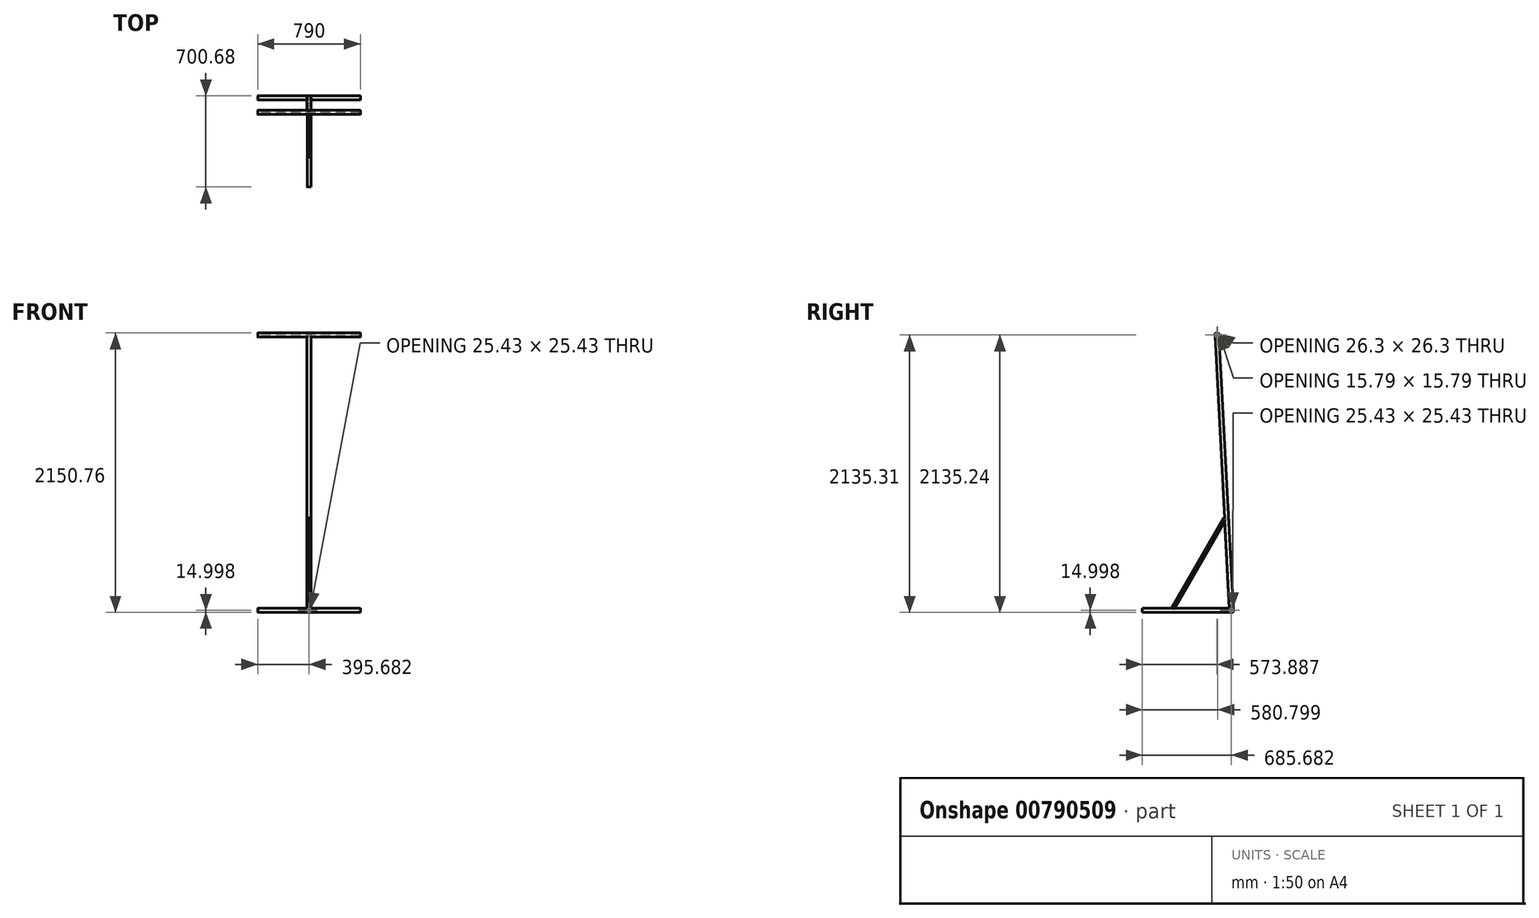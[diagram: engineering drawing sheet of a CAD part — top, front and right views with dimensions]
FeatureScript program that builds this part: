
annotation { "Feature Type Name" : "Feature", "Feature Type Description" : "" }
export const myFeature = defineFeature(function(context is Context, id is Id, definition is map)
    precondition{}
    {
        {
            var Q0;
            Q0=qCreatedBy(makeId("Top.planeOp"),FACE);
            var sketch = newSketch(context, id + "F0", { "sketchPlane" : qUnion([Q0])});
            skLineSegment(sketch, "E0.bottom", {"start": v(-8.65, 15) * mm, "end": v(8.65, 15) * mm});
            skLineSegment(sketch, "E0.top", {"start": v(-8.65, -15) * mm, "end": v(8.65, -15) * mm});
            skLineSegment(sketch, "E0.left", {"start": v(-15, 8.65) * mm, "end": v(-15, -8.65) * mm});
            skLineSegment(sketch, "E0.right", {"start": v(15, 8.65) * mm, "end": v(15, -8.65) * mm});
            skPoint(sketch, "E1", {"position": v(-15, 0) * mm});
            skPoint(sketch, "E2", {"position": v(0, 15) * mm});
            skPoint(sketch, "E3.visualSharp", {"position": v(-15, 15) * mm});
            skArc(sketch, "E3.filletArc", {"start": v(-8.65, 15) * mm, "mid": v(-13.14, 13.14) * mm, "end": v(-15, 8.65) * mm});
            skPoint(sketch, "E4.visualSharp", {"position": v(15, 15) * mm});
            skArc(sketch, "E4.filletArc", {"start": v(15, 8.65) * mm, "mid": v(13.14, 13.14) * mm, "end": v(8.65, 15) * mm});
            skPoint(sketch, "E5.visualSharp", {"position": v(15, -15) * mm});
            skArc(sketch, "E5.filletArc", {"start": v(8.65, -15) * mm, "mid": v(13.14, -13.14) * mm, "end": v(15, -8.65) * mm});
            skPoint(sketch, "E6.visualSharp", {"position": v(-15, -15) * mm});
            skArc(sketch, "E6.filletArc", {"start": v(-15, -8.65) * mm, "mid": v(-13.14, -13.14) * mm, "end": v(-8.65, -15) * mm});
            skArc(sketch, "E7.0", {"start": v(-8.65, 12.71) * mm, "mid": v(-11.52, 11.52) * mm, "end": v(-12.71, 8.65) * mm});
            skLineSegment(sketch, "E7.1", {"start": v(-8.65, 12.71) * mm, "end": v(8.65, 12.71) * mm});
            skLineSegment(sketch, "E7.2", {"start": v(-12.71, 8.65) * mm, "end": v(-12.71, -8.65) * mm});
            skArc(sketch, "E7.3", {"start": v(12.71, 8.65) * mm, "mid": v(11.52, 11.52) * mm, "end": v(8.65, 12.71) * mm});
            skArc(sketch, "E7.4", {"start": v(-12.71, -8.65) * mm, "mid": v(-11.52, -11.52) * mm, "end": v(-8.65, -12.71) * mm});
            skLineSegment(sketch, "E7.5", {"start": v(-8.65, -12.71) * mm, "end": v(8.65, -12.71) * mm});
            skArc(sketch, "E7.6", {"start": v(8.65, -12.71) * mm, "mid": v(11.52, -11.52) * mm, "end": v(12.71, -8.65) * mm});
            skLineSegment(sketch, "E7.7", {"start": v(12.71, 8.65) * mm, "end": v(12.71, -8.65) * mm});
            skSolve(sketch);
        }
        {
            var Q0;
            Q0=makeQuery(id+"F0.imprint","IMPRINT",FACE,{"disambiguationData":[TD([[makeQuery(id+"F0.imprint","IMPRINT",EDGE,{"derivedFrom":sQuery(id+"F0.wireOp",EDGE,"E0.bottom")}),-1.0]])]});
            extrude(context, id + "F1", {"entities" : qUnion([Q0]), "depth" : 2130 * mm, "offsetDistance" : 25.4 * mm});
        }
        {
            var Q0;
            Q0=makeQuery(id+"F1.opExtrude","SWEPT_BODY",BODY,{"disambiguationData":[OSD([sQuery(id+"F0.wireOp",EDGE,"E0.bottom"),sQuery(id+"F0.wireOp",EDGE,"E0.top"),sQuery(id+"F0.wireOp",EDGE,"E0.left"),sQuery(id+"F0.wireOp",EDGE,"E0.right"),sQuery(id+"F0.wireOp",EDGE,"E3.filletArc"),sQuery(id+"F0.wireOp",EDGE,"E4.filletArc"),sQuery(id+"F0.wireOp",EDGE,"E5.filletArc"),sQuery(id+"F0.wireOp",EDGE,"E6.filletArc"),sQuery(id+"F0.wireOp",EDGE,"E7.0"),sQuery(id+"F0.wireOp",EDGE,"E7.1"),sQuery(id+"F0.wireOp",EDGE,"E7.2"),sQuery(id+"F0.wireOp",EDGE,"E7.3"),sQuery(id+"F0.wireOp",EDGE,"E7.4"),sQuery(id+"F0.wireOp",EDGE,"E7.5"),sQuery(id+"F0.wireOp",EDGE,"E7.6"),sQuery(id+"F0.wireOp",EDGE,"E7.7")])]});
            var Q1;
            Q1=makeQuery(id+"F1.opExtrude","CAP_EDGE",EDGE,{"disambiguationData":[OSD([sQuery(id+"F0.wireOp",EDGE,"E0.top")])],"isStart":true});
            transform(context, id + "F2", {"entities" : qUnion([Q0]), "transformType" : TransformType.ROTATION, "transformAxis" : qUnion([Q1]), "angle" : 3 * degree, "makeCopy" : false});
        }
        {
            var Q0;
            Q0=qCreatedBy(makeId("Right.planeOp"),FACE);
            var sketch = newSketch(context, id + "F3", { "sketchPlane" : qUnion([Q0])});
            skLineSegment(sketch, "E8.bottom", {"start": v(-7.97, 14.32) * mm, "end": v(9.33, 14.32) * mm});
            skLineSegment(sketch, "E8.top", {"start": v(-7.97, -15.68) * mm, "end": v(9.33, -15.68) * mm});
            skLineSegment(sketch, "E8.left", {"start": v(-14.32, 7.97) * mm, "end": v(-14.32, -9.33) * mm});
            skLineSegment(sketch, "E8.right", {"start": v(15.68, 7.97) * mm, "end": v(15.68, -9.33) * mm});
            skPoint(sketch, "E9", {"position": v(-14.32, -0.68) * mm});
            skPoint(sketch, "E10", {"position": v(0.68, 14.32) * mm});
            skPoint(sketch, "E11.visualSharp", {"position": v(-14.32, 14.32) * mm});
            skArc(sketch, "E11.filletArc", {"start": v(-7.97, 14.32) * mm, "mid": v(-12.46, 12.46) * mm, "end": v(-14.32, 7.97) * mm});
            skPoint(sketch, "E12.visualSharp", {"position": v(15.68, 14.32) * mm});
            skArc(sketch, "E12.filletArc", {"start": v(15.68, 7.97) * mm, "mid": v(13.82, 12.46) * mm, "end": v(9.33, 14.32) * mm});
            skPoint(sketch, "E13.visualSharp", {"position": v(15.68, -15.68) * mm});
            skArc(sketch, "E13.filletArc", {"start": v(9.33, -15.68) * mm, "mid": v(13.82, -13.82) * mm, "end": v(15.68, -9.33) * mm});
            skPoint(sketch, "E14.visualSharp", {"position": v(-14.32, -15.68) * mm});
            skArc(sketch, "E14.filletArc", {"start": v(-14.32, -9.33) * mm, "mid": v(-12.46, -13.82) * mm, "end": v(-7.97, -15.68) * mm});
            skArc(sketch, "E15.0", {"start": v(-7.97, 12.03) * mm, "mid": v(-10.84, 10.84) * mm, "end": v(-12.03, 7.97) * mm});
            skLineSegment(sketch, "E15.1", {"start": v(-7.97, 12.03) * mm, "end": v(9.33, 12.03) * mm});
            skLineSegment(sketch, "E15.2", {"start": v(-12.03, 7.97) * mm, "end": v(-12.03, -9.33) * mm});
            skArc(sketch, "E15.3", {"start": v(13.4, 7.97) * mm, "mid": v(12.2, 10.84) * mm, "end": v(9.33, 12.03) * mm});
            skArc(sketch, "E15.4", {"start": v(-12.03, -9.33) * mm, "mid": v(-10.84, -12.2) * mm, "end": v(-7.97, -13.4) * mm});
            skLineSegment(sketch, "E15.5", {"start": v(-7.97, -13.4) * mm, "end": v(9.33, -13.4) * mm});
            skArc(sketch, "E15.6", {"start": v(9.33, -13.4) * mm, "mid": v(12.2, -12.2) * mm, "end": v(13.4, -9.33) * mm});
            skLineSegment(sketch, "E15.7", {"start": v(13.4, 7.97) * mm, "end": v(13.4, -9.33) * mm});
            skSolve(sketch);
        }
        {
            var Q0;
            Q0=makeQuery(id+"F3.imprint","IMPRINT",FACE,{"disambiguationData":[TD([[makeQuery(id+"F3.imprint","IMPRINT",EDGE,{"derivedFrom":sQuery(id+"F3.wireOp",EDGE,"E8.bottom")}),-1.0]])]});
            extrude(context, id + "F4", {"entities" : qUnion([Q0]), "depth" : 790 * mm, "offsetDistance" : 25.4 * mm});
        }
        {
            var Q0;
            Q0=makeQuery(id+"F4.opExtrude","SWEPT_BODY",BODY,{"disambiguationData":[OSD([sQuery(id+"F3.wireOp",EDGE,"E8.bottom"),sQuery(id+"F3.wireOp",EDGE,"E8.top"),sQuery(id+"F3.wireOp",EDGE,"E8.left"),sQuery(id+"F3.wireOp",EDGE,"E8.right"),sQuery(id+"F3.wireOp",EDGE,"E11.filletArc"),sQuery(id+"F3.wireOp",EDGE,"E12.filletArc"),sQuery(id+"F3.wireOp",EDGE,"E13.filletArc"),sQuery(id+"F3.wireOp",EDGE,"E14.filletArc"),sQuery(id+"F3.wireOp",EDGE,"E15.0"),sQuery(id+"F3.wireOp",EDGE,"E15.1"),sQuery(id+"F3.wireOp",EDGE,"E15.2"),sQuery(id+"F3.wireOp",EDGE,"E15.3"),sQuery(id+"F3.wireOp",EDGE,"E15.4"),sQuery(id+"F3.wireOp",EDGE,"E15.5"),sQuery(id+"F3.wireOp",EDGE,"E15.6"),sQuery(id+"F3.wireOp",EDGE,"E15.7")])]});
            transform(context, id + "F5", {"entities" : qUnion([Q0]), "transformType" : TransformType.TRANSLATION_3D, "dx" : -395 * mm, "dy" : 0 * mm, "dz" : 0 * mm, "makeCopy" : false});
        }
        {
            var Q0;
            Q0=makeQuery(id+"F4.opExtrude","SWEPT_BODY",BODY,{"disambiguationData":[OSD([sQuery(id+"F3.wireOp",EDGE,"E8.bottom"),sQuery(id+"F3.wireOp",EDGE,"E8.top"),sQuery(id+"F3.wireOp",EDGE,"E8.left"),sQuery(id+"F3.wireOp",EDGE,"E8.right"),sQuery(id+"F3.wireOp",EDGE,"E11.filletArc"),sQuery(id+"F3.wireOp",EDGE,"E12.filletArc"),sQuery(id+"F3.wireOp",EDGE,"E13.filletArc"),sQuery(id+"F3.wireOp",EDGE,"E14.filletArc"),sQuery(id+"F3.wireOp",EDGE,"E15.0"),sQuery(id+"F3.wireOp",EDGE,"E15.1"),sQuery(id+"F3.wireOp",EDGE,"E15.2"),sQuery(id+"F3.wireOp",EDGE,"E15.3"),sQuery(id+"F3.wireOp",EDGE,"E15.4"),sQuery(id+"F3.wireOp",EDGE,"E15.5"),sQuery(id+"F3.wireOp",EDGE,"E15.6"),sQuery(id+"F3.wireOp",EDGE,"E15.7")])]});
            transform(context, id + "F6", {"entities" : qUnion([Q0]), "transformType" : TransformType.TRANSLATION_3D, "dx" : 0 * mm, "dy" : 0 * mm, "dz" : 0 * mm, "makeCopy" : true});
        }
        {
            var Q0;
            Q0=makeQuery(id+"F6.opPattern","COPY",BODY,{"derivedFrom":makeQuery(id+"F4.opExtrude","SWEPT_BODY",BODY,{"disambiguationData":[OSD([sQuery(id+"F3.wireOp",EDGE,"E8.bottom"),sQuery(id+"F3.wireOp",EDGE,"E8.top"),sQuery(id+"F3.wireOp",EDGE,"E8.left"),sQuery(id+"F3.wireOp",EDGE,"E8.right"),sQuery(id+"F3.wireOp",EDGE,"E11.filletArc"),sQuery(id+"F3.wireOp",EDGE,"E12.filletArc"),sQuery(id+"F3.wireOp",EDGE,"E13.filletArc"),sQuery(id+"F3.wireOp",EDGE,"E14.filletArc"),sQuery(id+"F3.wireOp",EDGE,"E15.0"),sQuery(id+"F3.wireOp",EDGE,"E15.1"),sQuery(id+"F3.wireOp",EDGE,"E15.2"),sQuery(id+"F3.wireOp",EDGE,"E15.3"),sQuery(id+"F3.wireOp",EDGE,"E15.4"),sQuery(id+"F3.wireOp",EDGE,"E15.5"),sQuery(id+"F3.wireOp",EDGE,"E15.6"),sQuery(id+"F3.wireOp",EDGE,"E15.7")])]}),"instanceName":"1"});
            var Q1;
            Q1=makeQuery(id+"F6.opPattern","COPY",EDGE,{"derivedFrom":makeQuery(id+"F4.opExtrude","SWEPT_EDGE",EDGE,{"disambiguationData":[OSD([sQuery(id+"F3.wireOp",EDGE,"E8.top"),sQuery(id+"F3.wireOp",EDGE,"E14.filletArc")])]}),"instanceName":"1"});
            transform(context, id + "F7", {"entities" : qUnion([Q0]), "transformType" : TransformType.ROTATION, "transformAxis" : qUnion([Q1]), "angle" : 357 * degree, "makeCopy" : false});
        }
        {
            var Q0;
            Q0=makeQuery(id+"F6.opPattern","COPY",BODY,{"derivedFrom":makeQuery(id+"F4.opExtrude","SWEPT_BODY",BODY,{"disambiguationData":[OSD([sQuery(id+"F3.wireOp",EDGE,"E8.bottom"),sQuery(id+"F3.wireOp",EDGE,"E8.top"),sQuery(id+"F3.wireOp",EDGE,"E8.left"),sQuery(id+"F3.wireOp",EDGE,"E8.right"),sQuery(id+"F3.wireOp",EDGE,"E11.filletArc"),sQuery(id+"F3.wireOp",EDGE,"E12.filletArc"),sQuery(id+"F3.wireOp",EDGE,"E13.filletArc"),sQuery(id+"F3.wireOp",EDGE,"E14.filletArc"),sQuery(id+"F3.wireOp",EDGE,"E15.0"),sQuery(id+"F3.wireOp",EDGE,"E15.1"),sQuery(id+"F3.wireOp",EDGE,"E15.2"),sQuery(id+"F3.wireOp",EDGE,"E15.3"),sQuery(id+"F3.wireOp",EDGE,"E15.4"),sQuery(id+"F3.wireOp",EDGE,"E15.5"),sQuery(id+"F3.wireOp",EDGE,"E15.6"),sQuery(id+"F3.wireOp",EDGE,"E15.7")])]}),"instanceName":"1"});
            transform(context, id + "F8", {"entities" : qUnion([Q0]), "transformType" : TransformType.TRANSLATION_3D, "dx" : 0 * mm, "dy" : -111 * mm, "dz" : 2119.88 * mm, "makeCopy" : false});
        }
        {
            var Q0;
            Q0=qCreatedBy(makeId("Right.planeOp"),FACE);
            var sketch = newSketch(context, id + "F9", { "sketchPlane" : qUnion([Q0])});
            skLineSegment(sketch, "E16.bottom", {"start": v(2.03, 14.32) * mm, "end": v(9.33, 14.32) * mm});
            skLineSegment(sketch, "E16.top", {"start": v(2.03, -5.68) * mm, "end": v(9.33, -5.68) * mm});
            skLineSegment(sketch, "E16.left", {"start": v(-4.32, 7.97) * mm, "end": v(-4.32, 0.67) * mm});
            skLineSegment(sketch, "E16.right", {"start": v(15.68, 7.97) * mm, "end": v(15.68, 0.67) * mm});
            skPoint(sketch, "E17", {"position": v(-4.32, 4.32) * mm});
            skPoint(sketch, "E18", {"position": v(5.68, 14.32) * mm});
            skPoint(sketch, "E19.visualSharp", {"position": v(-4.32, 14.32) * mm});
            skArc(sketch, "E19.filletArc", {"start": v(2.03, 14.32) * mm, "mid": v(-2.46, 12.46) * mm, "end": v(-4.32, 7.97) * mm});
            skPoint(sketch, "E20.visualSharp", {"position": v(15.68, 14.32) * mm});
            skArc(sketch, "E20.filletArc", {"start": v(15.68, 7.97) * mm, "mid": v(13.82, 12.46) * mm, "end": v(9.33, 14.32) * mm});
            skPoint(sketch, "E21.visualSharp", {"position": v(15.68, -5.68) * mm});
            skArc(sketch, "E21.filletArc", {"start": v(9.33, -5.68) * mm, "mid": v(13.82, -3.82) * mm, "end": v(15.68, 0.67) * mm});
            skPoint(sketch, "E22.visualSharp", {"position": v(-4.32, -5.68) * mm});
            skArc(sketch, "E22.filletArc", {"start": v(-4.32, 0.67) * mm, "mid": v(-2.46, -3.82) * mm, "end": v(2.03, -5.68) * mm});
            skArc(sketch, "E23.0", {"start": v(2.03, 12.03) * mm, "mid": v(-0.84, 10.84) * mm, "end": v(-2.03, 7.97) * mm});
            skLineSegment(sketch, "E23.1", {"start": v(2.03, 12.03) * mm, "end": v(9.33, 12.03) * mm});
            skLineSegment(sketch, "E23.2", {"start": v(-2.03, 7.97) * mm, "end": v(-2.03, 0.67) * mm});
            skArc(sketch, "E23.3", {"start": v(13.4, 7.97) * mm, "mid": v(12.2, 10.84) * mm, "end": v(9.33, 12.03) * mm});
            skArc(sketch, "E23.4", {"start": v(-2.03, 0.67) * mm, "mid": v(-0.84, -2.2) * mm, "end": v(2.03, -3.4) * mm});
            skLineSegment(sketch, "E23.5", {"start": v(2.03, -3.4) * mm, "end": v(9.33, -3.4) * mm});
            skArc(sketch, "E23.6", {"start": v(9.33, -3.4) * mm, "mid": v(12.2, -2.2) * mm, "end": v(13.4, 0.67) * mm});
            skLineSegment(sketch, "E23.7", {"start": v(13.4, 7.97) * mm, "end": v(13.4, 0.67) * mm});
            skSolve(sketch);
        }
        {
            var Q0;
            Q0=makeQuery(id+"F9.imprint","IMPRINT",FACE,{"disambiguationData":[TD([[makeQuery(id+"F9.imprint","IMPRINT",EDGE,{"derivedFrom":sQuery(id+"F9.wireOp",EDGE,"E16.bottom")}),-1.0]])]});
            extrude(context, id + "F10", {"entities" : qUnion([Q0]), "depth" : 790 * mm, "offsetDistance" : 25.4 * mm});
        }
        {
            var Q0;
            Q0=makeQuery(id+"F10.opExtrude","SWEPT_BODY",BODY,{"disambiguationData":[OSD([sQuery(id+"F9.wireOp",EDGE,"E16.bottom"),sQuery(id+"F9.wireOp",EDGE,"E16.top"),sQuery(id+"F9.wireOp",EDGE,"E16.left"),sQuery(id+"F9.wireOp",EDGE,"E16.right"),sQuery(id+"F9.wireOp",EDGE,"E19.filletArc"),sQuery(id+"F9.wireOp",EDGE,"E20.filletArc"),sQuery(id+"F9.wireOp",EDGE,"E21.filletArc"),sQuery(id+"F9.wireOp",EDGE,"E22.filletArc"),sQuery(id+"F9.wireOp",EDGE,"E23.0"),sQuery(id+"F9.wireOp",EDGE,"E23.1"),sQuery(id+"F9.wireOp",EDGE,"E23.2"),sQuery(id+"F9.wireOp",EDGE,"E23.3"),sQuery(id+"F9.wireOp",EDGE,"E23.4"),sQuery(id+"F9.wireOp",EDGE,"E23.5"),sQuery(id+"F9.wireOp",EDGE,"E23.6"),sQuery(id+"F9.wireOp",EDGE,"E23.7")])]});
            transform(context, id + "F11", {"entities" : qUnion([Q0]), "transformType" : TransformType.TRANSLATION_3D, "dx" : -395 * mm, "dy" : 0 * mm, "dz" : 0 * mm, "makeCopy" : false});
        }
        {
            var Q0;
            Q0=makeQuery(id+"F10.opExtrude","SWEPT_BODY",BODY,{"disambiguationData":[OSD([sQuery(id+"F9.wireOp",EDGE,"E16.bottom"),sQuery(id+"F9.wireOp",EDGE,"E16.top"),sQuery(id+"F9.wireOp",EDGE,"E16.left"),sQuery(id+"F9.wireOp",EDGE,"E16.right"),sQuery(id+"F9.wireOp",EDGE,"E19.filletArc"),sQuery(id+"F9.wireOp",EDGE,"E20.filletArc"),sQuery(id+"F9.wireOp",EDGE,"E21.filletArc"),sQuery(id+"F9.wireOp",EDGE,"E22.filletArc"),sQuery(id+"F9.wireOp",EDGE,"E23.0"),sQuery(id+"F9.wireOp",EDGE,"E23.1"),sQuery(id+"F9.wireOp",EDGE,"E23.2"),sQuery(id+"F9.wireOp",EDGE,"E23.3"),sQuery(id+"F9.wireOp",EDGE,"E23.4"),sQuery(id+"F9.wireOp",EDGE,"E23.5"),sQuery(id+"F9.wireOp",EDGE,"E23.6"),sQuery(id+"F9.wireOp",EDGE,"E23.7")])]});
            transform(context, id + "F12", {"entities" : qUnion([Q0]), "transformType" : TransformType.TRANSLATION_3D, "dx" : 0 * mm, "dy" : -109.47 * mm, "dz" : 2115.06 * mm, "makeCopy" : false});
        }
        {
            var Q0;
            Q0=makeQuery(id+"F10.opExtrude","SWEPT_BODY",BODY,{"disambiguationData":[OSD([sQuery(id+"F9.wireOp",EDGE,"E16.bottom"),sQuery(id+"F9.wireOp",EDGE,"E16.top"),sQuery(id+"F9.wireOp",EDGE,"E16.left"),sQuery(id+"F9.wireOp",EDGE,"E16.right"),sQuery(id+"F9.wireOp",EDGE,"E19.filletArc"),sQuery(id+"F9.wireOp",EDGE,"E20.filletArc"),sQuery(id+"F9.wireOp",EDGE,"E21.filletArc"),sQuery(id+"F9.wireOp",EDGE,"E22.filletArc"),sQuery(id+"F9.wireOp",EDGE,"E23.0"),sQuery(id+"F9.wireOp",EDGE,"E23.1"),sQuery(id+"F9.wireOp",EDGE,"E23.2"),sQuery(id+"F9.wireOp",EDGE,"E23.3"),sQuery(id+"F9.wireOp",EDGE,"E23.4"),sQuery(id+"F9.wireOp",EDGE,"E23.5"),sQuery(id+"F9.wireOp",EDGE,"E23.6"),sQuery(id+"F9.wireOp",EDGE,"E23.7")])]});
            var Q1;
            Q1=makeQuery(id+"F10.opExtrude","SWEPT_EDGE",EDGE,{"disambiguationData":[OSD([sQuery(id+"F9.wireOp",EDGE,"E23.4"),sQuery(id+"F9.wireOp",EDGE,"E23.5")])]});
            transform(context, id + "F13", {"entities" : qUnion([Q0]), "transformType" : TransformType.ROTATION, "transformAxis" : qUnion([Q1]), "angle" : 357 * degree, "makeCopy" : false});
        }
        {
            var Q0;
            Q0=qCreatedBy(makeId("Front.planeOp"),FACE);
            var sketch = newSketch(context, id + "F14", { "sketchPlane" : qUnion([Q0])});
            skLineSegment(sketch, "E24.bottom", {"start": v(-7.97, 14.32) * mm, "end": v(9.33, 14.32) * mm});
            skLineSegment(sketch, "E24.top", {"start": v(-7.97, -15.68) * mm, "end": v(9.33, -15.68) * mm});
            skLineSegment(sketch, "E24.left", {"start": v(-14.32, 7.97) * mm, "end": v(-14.32, -9.33) * mm});
            skLineSegment(sketch, "E24.right", {"start": v(15.68, 7.97) * mm, "end": v(15.68, -9.33) * mm});
            skPoint(sketch, "E25", {"position": v(-14.32, -0.68) * mm});
            skPoint(sketch, "E26", {"position": v(0.68, 14.32) * mm});
            skPoint(sketch, "E27.visualSharp", {"position": v(-14.32, 14.32) * mm});
            skArc(sketch, "E27.filletArc", {"start": v(-7.97, 14.32) * mm, "mid": v(-12.46, 12.46) * mm, "end": v(-14.32, 7.97) * mm});
            skPoint(sketch, "E28.visualSharp", {"position": v(15.68, 14.32) * mm});
            skArc(sketch, "E28.filletArc", {"start": v(15.68, 7.97) * mm, "mid": v(13.82, 12.46) * mm, "end": v(9.33, 14.32) * mm});
            skPoint(sketch, "E29.visualSharp", {"position": v(15.68, -15.68) * mm});
            skArc(sketch, "E29.filletArc", {"start": v(9.33, -15.68) * mm, "mid": v(13.82, -13.82) * mm, "end": v(15.68, -9.33) * mm});
            skPoint(sketch, "E30.visualSharp", {"position": v(-14.32, -15.68) * mm});
            skArc(sketch, "E30.filletArc", {"start": v(-14.32, -9.33) * mm, "mid": v(-12.46, -13.82) * mm, "end": v(-7.97, -15.68) * mm});
            skArc(sketch, "E31.0", {"start": v(-7.97, 12.03) * mm, "mid": v(-10.84, 10.84) * mm, "end": v(-12.03, 7.97) * mm});
            skLineSegment(sketch, "E31.1", {"start": v(-7.97, 12.03) * mm, "end": v(9.33, 12.03) * mm});
            skLineSegment(sketch, "E31.2", {"start": v(-12.03, 7.97) * mm, "end": v(-12.03, -9.33) * mm});
            skArc(sketch, "E31.3", {"start": v(13.4, 7.97) * mm, "mid": v(12.2, 10.84) * mm, "end": v(9.33, 12.03) * mm});
            skArc(sketch, "E31.4", {"start": v(-12.03, -9.33) * mm, "mid": v(-10.84, -12.2) * mm, "end": v(-7.97, -13.4) * mm});
            skLineSegment(sketch, "E31.5", {"start": v(-7.97, -13.4) * mm, "end": v(9.33, -13.4) * mm});
            skArc(sketch, "E31.6", {"start": v(9.33, -13.4) * mm, "mid": v(12.2, -12.2) * mm, "end": v(13.4, -9.33) * mm});
            skLineSegment(sketch, "E31.7", {"start": v(13.4, 7.97) * mm, "end": v(13.4, -9.33) * mm});
            skSolve(sketch);
        }
        {
            var Q0;
            Q0=makeQuery(id+"F14.imprint","IMPRINT",FACE,{"disambiguationData":[TD([[makeQuery(id+"F14.imprint","IMPRINT",EDGE,{"derivedFrom":sQuery(id+"F14.wireOp",EDGE,"E24.bottom")}),-1.0]])]});
            extrude(context, id + "F15", {"entities" : qUnion([Q0]), "depth" : 685 * mm, "offsetDistance" : 25.4 * mm});
        }
        {
            var Q0;
            Q0=qCreatedBy(makeId("Front.planeOp"),FACE);
            var sketch = newSketch(context, id + "F16", { "sketchPlane" : qUnion([Q0])});
            skLineSegment(sketch, "E32.bottom", {"start": v(-3.2, 9.55) * mm, "end": v(4.1, 9.55) * mm});
            skLineSegment(sketch, "E32.top", {"start": v(-3.2, -10.45) * mm, "end": v(4.1, -10.45) * mm});
            skLineSegment(sketch, "E32.left", {"start": v(-9.55, 3.2) * mm, "end": v(-9.55, -4.1) * mm});
            skLineSegment(sketch, "E32.right", {"start": v(10.45, 3.2) * mm, "end": v(10.45, -4.1) * mm});
            skPoint(sketch, "E33", {"position": v(-9.55, -0.45) * mm});
            skPoint(sketch, "E34", {"position": v(0.45, 9.55) * mm});
            skPoint(sketch, "E35.visualSharp", {"position": v(-9.55, 9.55) * mm});
            skArc(sketch, "E35.filletArc", {"start": v(-3.2, 9.55) * mm, "mid": v(-7.69, 7.69) * mm, "end": v(-9.55, 3.2) * mm});
            skPoint(sketch, "E36.visualSharp", {"position": v(10.45, 9.55) * mm});
            skArc(sketch, "E36.filletArc", {"start": v(10.45, 3.2) * mm, "mid": v(8.6, 7.69) * mm, "end": v(4.1, 9.55) * mm});
            skPoint(sketch, "E37.visualSharp", {"position": v(10.45, -10.45) * mm});
            skArc(sketch, "E37.filletArc", {"start": v(4.1, -10.45) * mm, "mid": v(8.6, -8.6) * mm, "end": v(10.45, -4.1) * mm});
            skPoint(sketch, "E38.visualSharp", {"position": v(-9.55, -10.45) * mm});
            skArc(sketch, "E38.filletArc", {"start": v(-9.55, -4.1) * mm, "mid": v(-7.69, -8.6) * mm, "end": v(-3.2, -10.45) * mm});
            skArc(sketch, "E39.0", {"start": v(-3.2, 7.26) * mm, "mid": v(-6.07, 6.07) * mm, "end": v(-7.26, 3.2) * mm});
            skLineSegment(sketch, "E39.1", {"start": v(-3.2, 7.26) * mm, "end": v(4.1, 7.26) * mm});
            skLineSegment(sketch, "E39.2", {"start": v(-7.26, 3.2) * mm, "end": v(-7.26, -4.1) * mm});
            skArc(sketch, "E39.3", {"start": v(8.17, 3.2) * mm, "mid": v(6.98, 6.07) * mm, "end": v(4.1, 7.26) * mm});
            skArc(sketch, "E39.4", {"start": v(-7.26, -4.1) * mm, "mid": v(-6.07, -6.98) * mm, "end": v(-3.2, -8.17) * mm});
            skLineSegment(sketch, "E39.5", {"start": v(-3.2, -8.17) * mm, "end": v(4.1, -8.17) * mm});
            skArc(sketch, "E39.6", {"start": v(4.1, -8.17) * mm, "mid": v(6.98, -6.98) * mm, "end": v(8.17, -4.1) * mm});
            skLineSegment(sketch, "E39.7", {"start": v(8.17, 3.2) * mm, "end": v(8.17, -4.1) * mm});
            skSolve(sketch);
        }
        {
            var Q0;
            Q0=makeQuery(id+"F16.imprint","IMPRINT",FACE,{"disambiguationData":[TD([[makeQuery(id+"F16.imprint","IMPRINT",EDGE,{"derivedFrom":sQuery(id+"F16.wireOp",EDGE,"E32.bottom")}),-1.0]])]});
            extrude(context, id + "F17", {"entities" : qUnion([Q0]), "depth" : 800 * mm, "offsetDistance" : 25.4 * mm});
        }
        {
            var Q0;
            Q0=makeQuery(id+"F17.opExtrude","SWEPT_BODY",BODY,{"disambiguationData":[OSD([sQuery(id+"F16.wireOp",EDGE,"E32.bottom"),sQuery(id+"F16.wireOp",EDGE,"E32.top"),sQuery(id+"F16.wireOp",EDGE,"E32.left"),sQuery(id+"F16.wireOp",EDGE,"E32.right"),sQuery(id+"F16.wireOp",EDGE,"E35.filletArc"),sQuery(id+"F16.wireOp",EDGE,"E36.filletArc"),sQuery(id+"F16.wireOp",EDGE,"E37.filletArc"),sQuery(id+"F16.wireOp",EDGE,"E38.filletArc"),sQuery(id+"F16.wireOp",EDGE,"E39.0"),sQuery(id+"F16.wireOp",EDGE,"E39.1"),sQuery(id+"F16.wireOp",EDGE,"E39.2"),sQuery(id+"F16.wireOp",EDGE,"E39.3"),sQuery(id+"F16.wireOp",EDGE,"E39.4"),sQuery(id+"F16.wireOp",EDGE,"E39.5"),sQuery(id+"F16.wireOp",EDGE,"E39.6"),sQuery(id+"F16.wireOp",EDGE,"E39.7")])]});
            var Q1;
            Q1=makeQuery(id+"F17.opExtrude","CAP_EDGE",EDGE,{"disambiguationData":[OSD([sQuery(id+"F16.wireOp",EDGE,"E32.bottom")])],"isStart":true});
            transform(context, id + "F18", {"entities" : qUnion([Q0]), "transformType" : TransformType.ROTATION, "transformAxis" : qUnion([Q1]), "angle" : 120 * degree, "oppositeDirection" : true, "makeCopy" : false});
        }
        {
            var Q0;
            Q0=makeQuery(id+"F17.opExtrude","SWEPT_BODY",BODY,{"disambiguationData":[OSD([sQuery(id+"F16.wireOp",EDGE,"E32.bottom"),sQuery(id+"F16.wireOp",EDGE,"E32.top"),sQuery(id+"F16.wireOp",EDGE,"E32.left"),sQuery(id+"F16.wireOp",EDGE,"E32.right"),sQuery(id+"F16.wireOp",EDGE,"E35.filletArc"),sQuery(id+"F16.wireOp",EDGE,"E36.filletArc"),sQuery(id+"F16.wireOp",EDGE,"E37.filletArc"),sQuery(id+"F16.wireOp",EDGE,"E38.filletArc"),sQuery(id+"F16.wireOp",EDGE,"E39.0"),sQuery(id+"F16.wireOp",EDGE,"E39.1"),sQuery(id+"F16.wireOp",EDGE,"E39.2"),sQuery(id+"F16.wireOp",EDGE,"E39.3"),sQuery(id+"F16.wireOp",EDGE,"E39.4"),sQuery(id+"F16.wireOp",EDGE,"E39.5"),sQuery(id+"F16.wireOp",EDGE,"E39.6"),sQuery(id+"F16.wireOp",EDGE,"E39.7")])]});
            transform(context, id + "F19", {"entities" : qUnion([Q0]), "transformType" : TransformType.TRANSLATION_3D, "dx" : 0 * mm, "dy" : -439.42 * mm, "dz" : 0 * mm, "makeCopy" : false});
        }
    });
